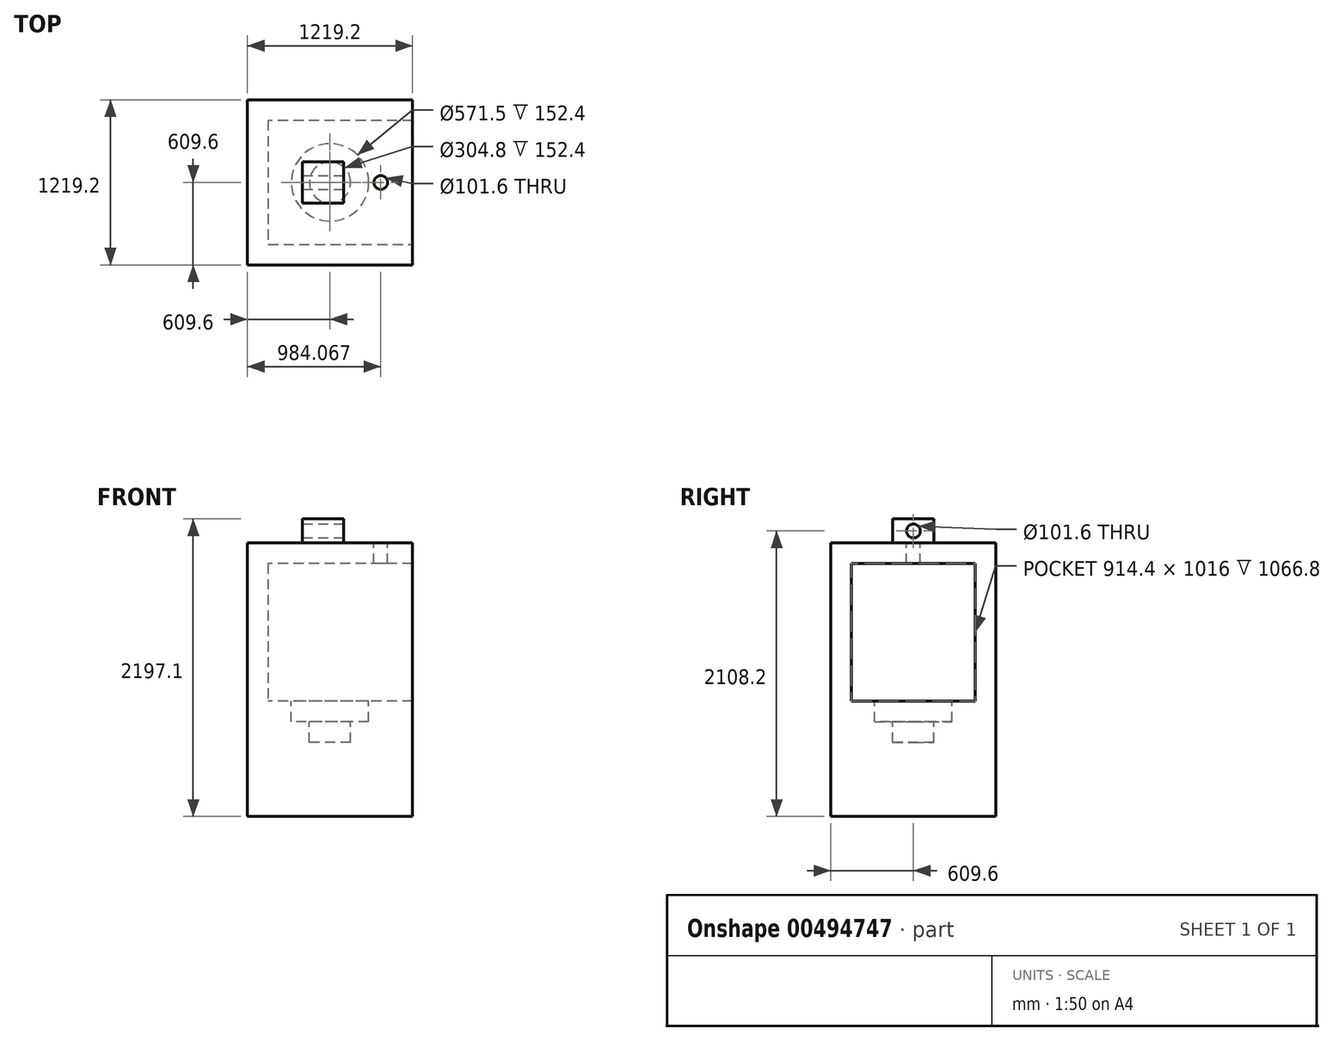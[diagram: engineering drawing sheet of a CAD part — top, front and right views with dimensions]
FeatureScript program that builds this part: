
annotation { "Feature Type Name" : "Feature", "Feature Type Description" : "" }
export const myFeature = defineFeature(function(context is Context, id is Id, definition is map)
    precondition{}
    {
        {
            var Q0;
            Q0=qCreatedBy(makeId("Top.planeOp"),FACE);
            var sketch = newSketch(context, id + "F0", { "sketchPlane" : qUnion([Q0])});
            skLineSegment(sketch, "E0.bottom", {"start": v(-609.6, 609.6) * mm, "end": v(609.6, 609.6) * mm});
            skLineSegment(sketch, "E0.top", {"start": v(-609.6, -609.6) * mm, "end": v(609.6, -609.6) * mm});
            skLineSegment(sketch, "E0.left", {"start": v(-609.6, 609.6) * mm, "end": v(-609.6, -609.6) * mm});
            skLineSegment(sketch, "E0.right", {"start": v(609.6, 609.6) * mm, "end": v(609.6, -609.6) * mm});
            skPoint(sketch, "E0.middle", {"position": v(0, 0) * mm});
            skSolve(sketch);
        }
        {
            var Q0;
            Q0 = qSketchRegion(id + "F0", true);
            extrude(context, id + "F1", {"entities" : qUnion([Q0]), "depth" : 850.9 * mm});
        }
        {
            var Q0;
            Q0=makeQuery(id+"F1.opExtrude","CAP_FACE",FACE,{"disambiguationData":[OSD([sQuery(id+"F0.wireOp",EDGE,"E0.bottom"),sQuery(id+"F0.wireOp",EDGE,"E0.top"),sQuery(id+"F0.wireOp",EDGE,"E0.left"),sQuery(id+"F0.wireOp",EDGE,"E0.right")])],"isStart":false});
            var sketch = newSketch(context, id + "F2", { "sketchPlane" : qUnion([Q0])});
            skCircle(sketch, "E1", {"center": v(0, 0) * mm, "radius": 152.4 * mm});
            skSolve(sketch);
        }
        {
            var Q0;
            Q0 = qSketchRegion(id + "F2", true);
            extrude(context, id + "F3", {"entities" : qUnion([Q0]), "operationType" : NewBodyOperationType.REMOVE, "oppositeDirection" : true, "depth" : 304.8 * mm});
        }
        {
            var Q0;
            Q0=makeQuery(id+"F1.opExtrude","CAP_FACE",FACE,{"disambiguationData":[OSD([sQuery(id+"F0.wireOp",EDGE,"E0.bottom"),sQuery(id+"F0.wireOp",EDGE,"E0.top"),sQuery(id+"F0.wireOp",EDGE,"E0.left"),sQuery(id+"F0.wireOp",EDGE,"E0.right")])],"isStart":false});
            var sketch = newSketch(context, id + "F4", { "sketchPlane" : qUnion([Q0])});
            skCircle(sketch, "E2", {"center": v(0, 0) * mm, "radius": 285.75 * mm});
            skSolve(sketch);
        }
        {
            var Q0;
            Q0 = qSketchRegion(id + "F4", true);
            extrude(context, id + "F5", {"entities" : qUnion([Q0]), "operationType" : NewBodyOperationType.REMOVE, "oppositeDirection" : true, "depth" : 152.4 * mm});
        }
        {
            var Q0;
            Q0=makeQuery(id+"F1.opExtrude","CAP_FACE",FACE,{"disambiguationData":[OSD([sQuery(id+"F0.wireOp",EDGE,"E0.bottom"),sQuery(id+"F0.wireOp",EDGE,"E0.top"),sQuery(id+"F0.wireOp",EDGE,"E0.left"),sQuery(id+"F0.wireOp",EDGE,"E0.right")])],"isStart":false});
            var sketch = newSketch(context, id + "F6", { "sketchPlane" : qUnion([Q0])});
            skLineSegment(sketch, "E3", {"start": v(609.6, -609.6) * mm, "end": v(609.6, -457.2) * mm});
            skLineSegment(sketch, "E4", {"start": v(609.6, -609.6) * mm, "end": v(-609.6, -609.6) * mm});
            skLineSegment(sketch, "E5", {"start": v(-609.6, -609.6) * mm, "end": v(-609.6, 609.6) * mm});
            skLineSegment(sketch, "E6", {"start": v(-609.6, 609.6) * mm, "end": v(609.6, 609.6) * mm});
            skLineSegment(sketch, "E7", {"start": v(609.6, 609.6) * mm, "end": v(609.6, 457.2) * mm});
            skLineSegment(sketch, "E8", {"start": v(609.6, 457.2) * mm, "end": v(-457.2, 457.2) * mm});
            skLineSegment(sketch, "E9", {"start": v(-457.2, 457.2) * mm, "end": v(-457.2, -457.2) * mm});
            skLineSegment(sketch, "E10", {"start": v(-457.2, -457.2) * mm, "end": v(609.6, -457.2) * mm});
            skSolve(sketch);
        }
        {
            var Q0;
            Q0 = qSketchRegion(id + "F6", true);
            extrude(context, id + "F7", {"entities" : qUnion([Q0]), "operationType" : NewBodyOperationType.ADD, "depth" : 1016 * mm});
        }
        {
            var Q0;
            Q0=makeQuery(id+"F7.opExtrude","CAP_FACE",FACE,{"disambiguationData":[OSD([sQuery(id+"F6.wireOp",EDGE,"E3"),sQuery(id+"F6.wireOp",EDGE,"E4"),sQuery(id+"F6.wireOp",EDGE,"E5"),sQuery(id+"F6.wireOp",EDGE,"E6"),sQuery(id+"F6.wireOp",EDGE,"E7"),sQuery(id+"F6.wireOp",EDGE,"E8"),sQuery(id+"F6.wireOp",EDGE,"E9"),sQuery(id+"F6.wireOp",EDGE,"E10")])],"isStart":false});
            var sketch = newSketch(context, id + "F8", { "sketchPlane" : qUnion([Q0])});
            skLineSegment(sketch, "E11.bottom", {"start": v(-609.6, 609.6) * mm, "end": v(609.6, 609.6) * mm});
            skLineSegment(sketch, "E11.top", {"start": v(-609.6, -609.6) * mm, "end": v(609.6, -609.6) * mm});
            skLineSegment(sketch, "E11.left", {"start": v(-609.6, 609.6) * mm, "end": v(-609.6, -609.6) * mm});
            skLineSegment(sketch, "E11.right", {"start": v(609.6, 609.6) * mm, "end": v(609.6, -609.6) * mm});
            skSolve(sketch);
        }
        {
            var Q0;
            Q0 = qSketchRegion(id + "F8", true);
            extrude(context, id + "F9", {"entities" : qUnion([Q0]), "operationType" : NewBodyOperationType.ADD, "depth" : 152.4 * mm});
        }
        {
            var Q0;
            Q0=makeQuery(id+"F9.opExtrude","CAP_FACE",FACE,{"disambiguationData":[OSD([sQuery(id+"F8.wireOp",EDGE,"E11.bottom"),sQuery(id+"F8.wireOp",EDGE,"E11.top"),sQuery(id+"F8.wireOp",EDGE,"E11.left"),sQuery(id+"F8.wireOp",EDGE,"E11.right")])],"isStart":false});
            var sketch = newSketch(context, id + "F10", { "sketchPlane" : qUnion([Q0])});
            skLineSegment(sketch, "E12.bottom", {"start": v(101.6, -152.4) * mm, "end": v(-101.6, -152.4) * mm});
            skLineSegment(sketch, "E12.top", {"start": v(101.6, 152.4) * mm, "end": v(-101.6, 152.4) * mm});
            skLineSegment(sketch, "E12.left", {"start": v(101.6, -152.4) * mm, "end": v(101.6, 152.4) * mm});
            skLineSegment(sketch, "E12.right", {"start": v(-101.6, -152.4) * mm, "end": v(-101.6, 152.4) * mm});
            skPoint(sketch, "E12.middle", {"position": v(0, 0) * mm});
            skSolve(sketch);
        }
        {
            var Q0;
            Q0 = qSketchRegion(id + "F10", true);
            extrude(context, id + "F11", {"entities" : qUnion([Q0]), "operationType" : NewBodyOperationType.ADD, "depth" : 177.8 * mm});
        }
        {
            var Q0;
            Q0=makeQuery(id+"F11.opExtrude","SWEPT_FACE",FACE,{"disambiguationData":[OSD([sQuery(id+"F10.wireOp",EDGE,"E12.left")])]});
            var sketch = newSketch(context, id + "F12", { "sketchPlane" : qUnion([Q0])});
            skCircle(sketch, "E13", {"center": v(0, 2108.2) * mm, "radius": 50.8 * mm});
            skPoint(sketch, "E13.centerSnap0", {"position": v(-152.4, 2108.2) * mm});
            skSolve(sketch);
        }
        {
            var Q0;
            Q0 = qSketchRegion(id + "F12", true);
            extrude(context, id + "F13", {"entities" : qUnion([Q0]), "operationType" : NewBodyOperationType.REMOVE, "oppositeDirection" : true, "depth" : 622.3 * mm});
        }
        {
            var Q0;
            Q0=makeQuery(id+"F9.opExtrude","CAP_FACE",FACE,{"disambiguationData":[OSD([sQuery(id+"F8.wireOp",EDGE,"E11.bottom"),sQuery(id+"F8.wireOp",EDGE,"E11.top"),sQuery(id+"F8.wireOp",EDGE,"E11.left"),sQuery(id+"F8.wireOp",EDGE,"E11.right")])],"isStart":false});
            var sketch = newSketch(context, id + "F14", { "sketchPlane" : qUnion([Q0])});
            skSolve(sketch);
        }
        {
            var Q0;
            Q0=makeQuery(id+"F11.opExtrude","SWEPT_FACE",FACE,{"disambiguationData":[OSD([sQuery(id+"F10.wireOp",EDGE,"E12.left")])]});
            extrude(context, id + "F15", {"entities" : qUnion([Q0]), "operationType" : NewBodyOperationType.ADD, "oppositeDirection" : true, "depth" : 304.8 * mm});
        }
        {
            var Q0;
            Q0=makeQuery(id+"F14.imprint","IMPRINT",FACE,{"disambiguationData":[TD([[makeQuery(id+"F14.imprint","IMPRINT",EDGE,{"derivedFrom":makeQuery(id+"F9.opExtrude","CAP_EDGE",EDGE,{"disambiguationData":[OSD([sQuery(id+"F8.wireOp",EDGE,"E11.bottom")])],"isStart":false})}),-1.0]])]});
            var sketch = newSketch(context, id + "F16", { "sketchPlane" : qUnion([Q0])});
            skCircle(sketch, "E14", {"center": v(374.47, 0) * mm, "radius": 50.8 * mm});
            skSolve(sketch);
        }
        {
            var Q0;
            Q0 = qSketchRegion(id + "F16", true);
            extrude(context, id + "F17", {"entities" : qUnion([Q0]), "operationType" : NewBodyOperationType.REMOVE, "oppositeDirection" : true, "depth" : 304.8 * mm});
        }
    });
